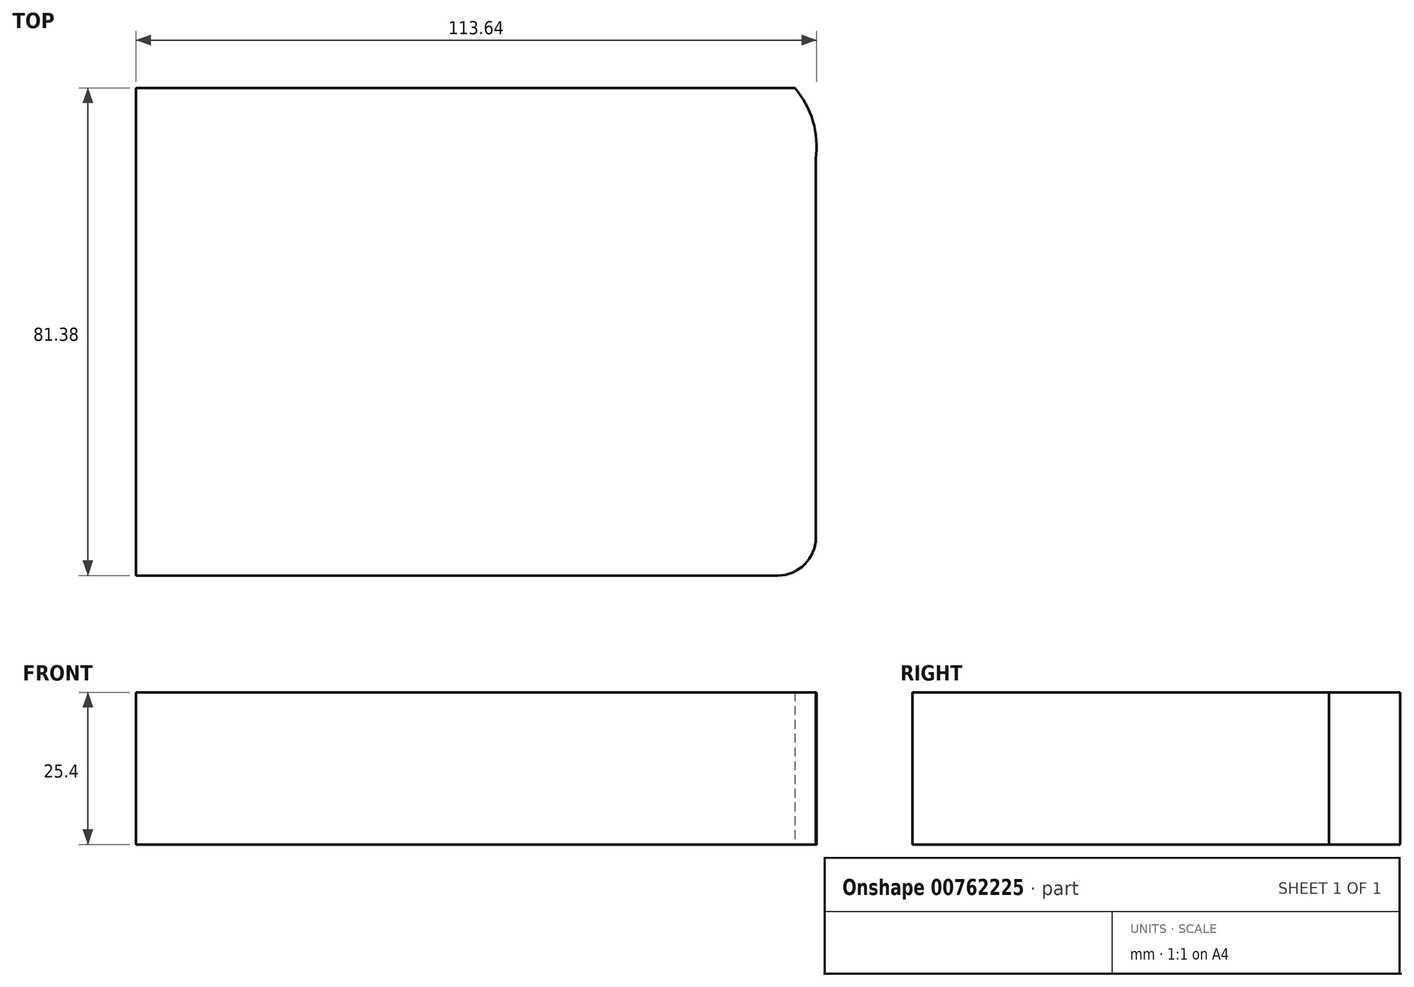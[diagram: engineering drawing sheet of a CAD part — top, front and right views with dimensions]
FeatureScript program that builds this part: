
annotation { "Feature Type Name" : "Feature", "Feature Type Description" : "" }
export const myFeature = defineFeature(function(context is Context, id is Id, definition is map)
    precondition{}
    {
        {
            var Q0;
            Q0=qCreatedBy(makeId("Top.planeOp"),FACE);
            var sketch = newSketch(context, id + "F0", { "sketchPlane" : qUnion([Q0])});
            skPoint(sketch, "E0.middle", {"position": v(0, 0) * mm});
            skLineSegment(sketch, "E1.bottom", {"start": v(-61.61, 43.4) * mm, "end": v(48.39, 43.4) * mm});
            skLineSegment(sketch, "E1.top", {"start": v(-61.61, -38) * mm, "end": v(45.55, -38) * mm});
            skLineSegment(sketch, "E1.left", {"start": v(-61.61, 43.4) * mm, "end": v(-61.61, -38) * mm});
            skLineSegment(sketch, "E1.right", {"start": v(51.9, 35.53) * mm, "end": v(51.9, -31.64) * mm});
            skArc(sketch, "E2", {"start": v(25.37, 43.4) * mm, "mid": v(36.88, 18.4) * mm, "end": v(48.39, 43.4) * mm});
            skPoint(sketch, "E3", {"position": v(25.37, 43.4) * mm});
            skPoint(sketch, "E4", {"position": v(47.21, 44.62) * mm});
            skPoint(sketch, "E5", {"position": v(48.39, 43.4) * mm});
            skPoint(sketch, "E6.visualSharp", {"position": v(51.9, -38) * mm});
            skArc(sketch, "E6.filletArc", {"start": v(45.55, -38) * mm, "mid": v(50.04, -36.13) * mm, "end": v(51.9, -31.64) * mm});
            skSolve(sketch);
        }
        {
            var Q0;
            Q0 = qSketchRegion(id + "F0", true);
            extrude(context, id + "F1", {"entities" : qUnion([Q0]), "depth" : 25.4 * mm, "offsetDistance" : 25.4 * mm});
        }
    });
